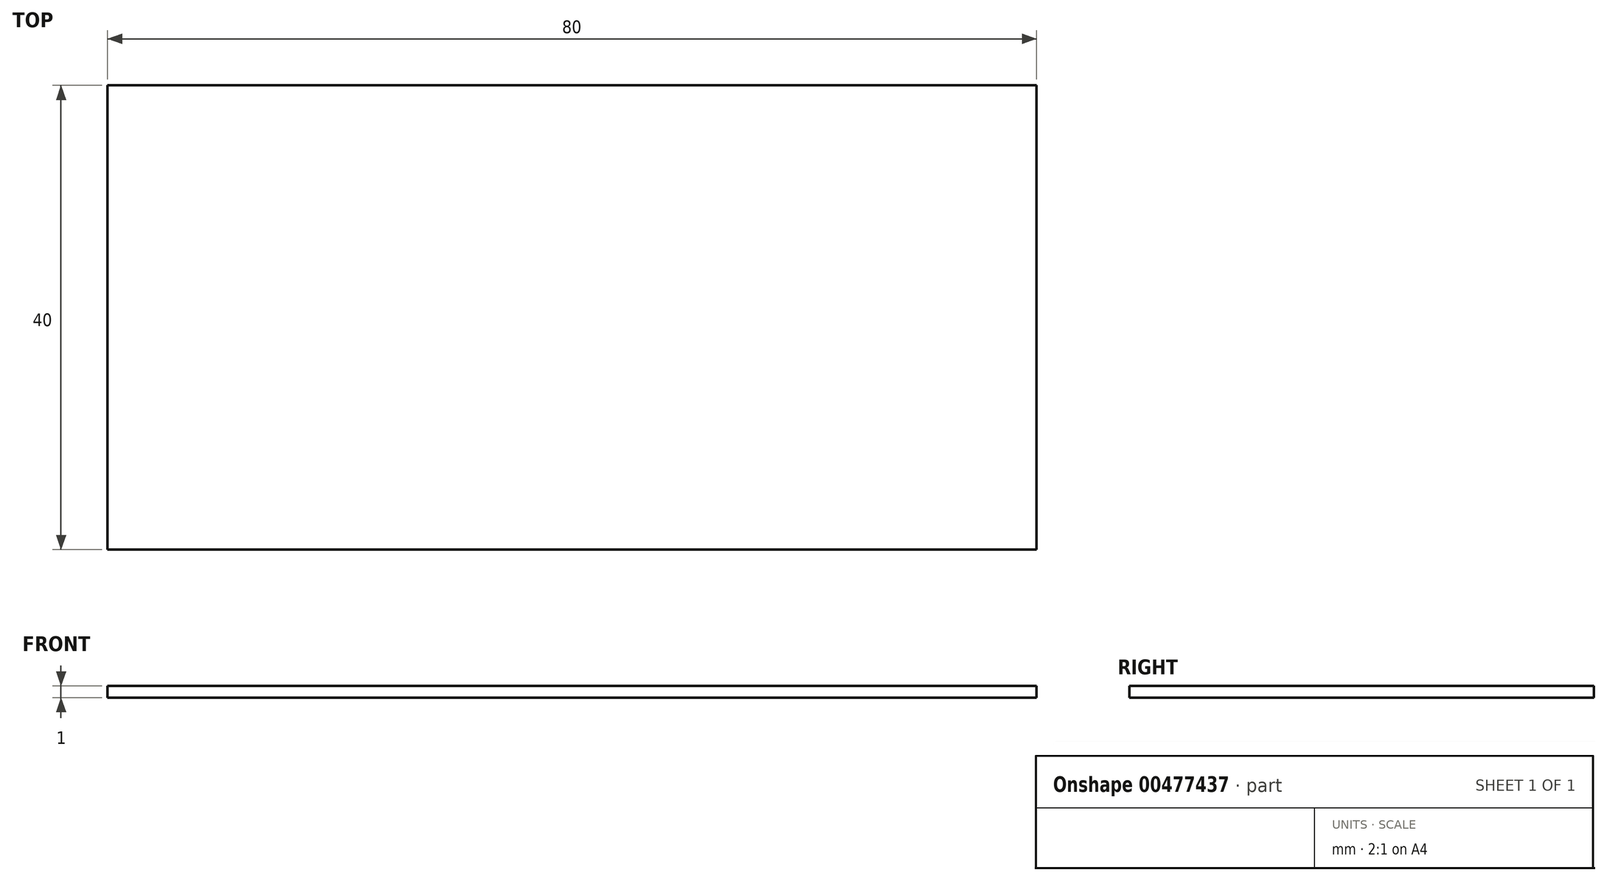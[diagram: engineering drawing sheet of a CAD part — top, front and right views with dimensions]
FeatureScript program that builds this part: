
annotation { "Feature Type Name" : "Feature", "Feature Type Description" : "" }
export const myFeature = defineFeature(function(context is Context, id is Id, definition is map)
    precondition{}
    {
        {
            var Q0;
            Q0=qCreatedBy(makeId("Top.planeOp"),FACE);
            var sketch = newSketch(context, id + "F0", { "sketchPlane" : qUnion([Q0])});
            skLineSegment(sketch, "E0.bottom", {"start": v(-80, 0) * mm, "end": v(0, 0) * mm});
            skLineSegment(sketch, "E0.top", {"start": v(-80, 40) * mm, "end": v(0, 40) * mm});
            skLineSegment(sketch, "E0.left", {"start": v(-80, 0) * mm, "end": v(-80, 40) * mm});
            skLineSegment(sketch, "E0.right", {"start": v(0, 0) * mm, "end": v(0, 40) * mm});
            skSolve(sketch);
        }
        {
            var Q0;
            Q0=makeQuery(id+"F0.imprint","IMPRINT",FACE,{"disambiguationData":[TD([[makeQuery(id+"F0.imprint","IMPRINT",EDGE,{"derivedFrom":sQuery(id+"F0.wireOp",EDGE,"E0.bottom")}),1.0]])]});
            extrude(context, id + "F1", {"entities" : qUnion([Q0]), "depth" : 1 * mm});
        }
    });
